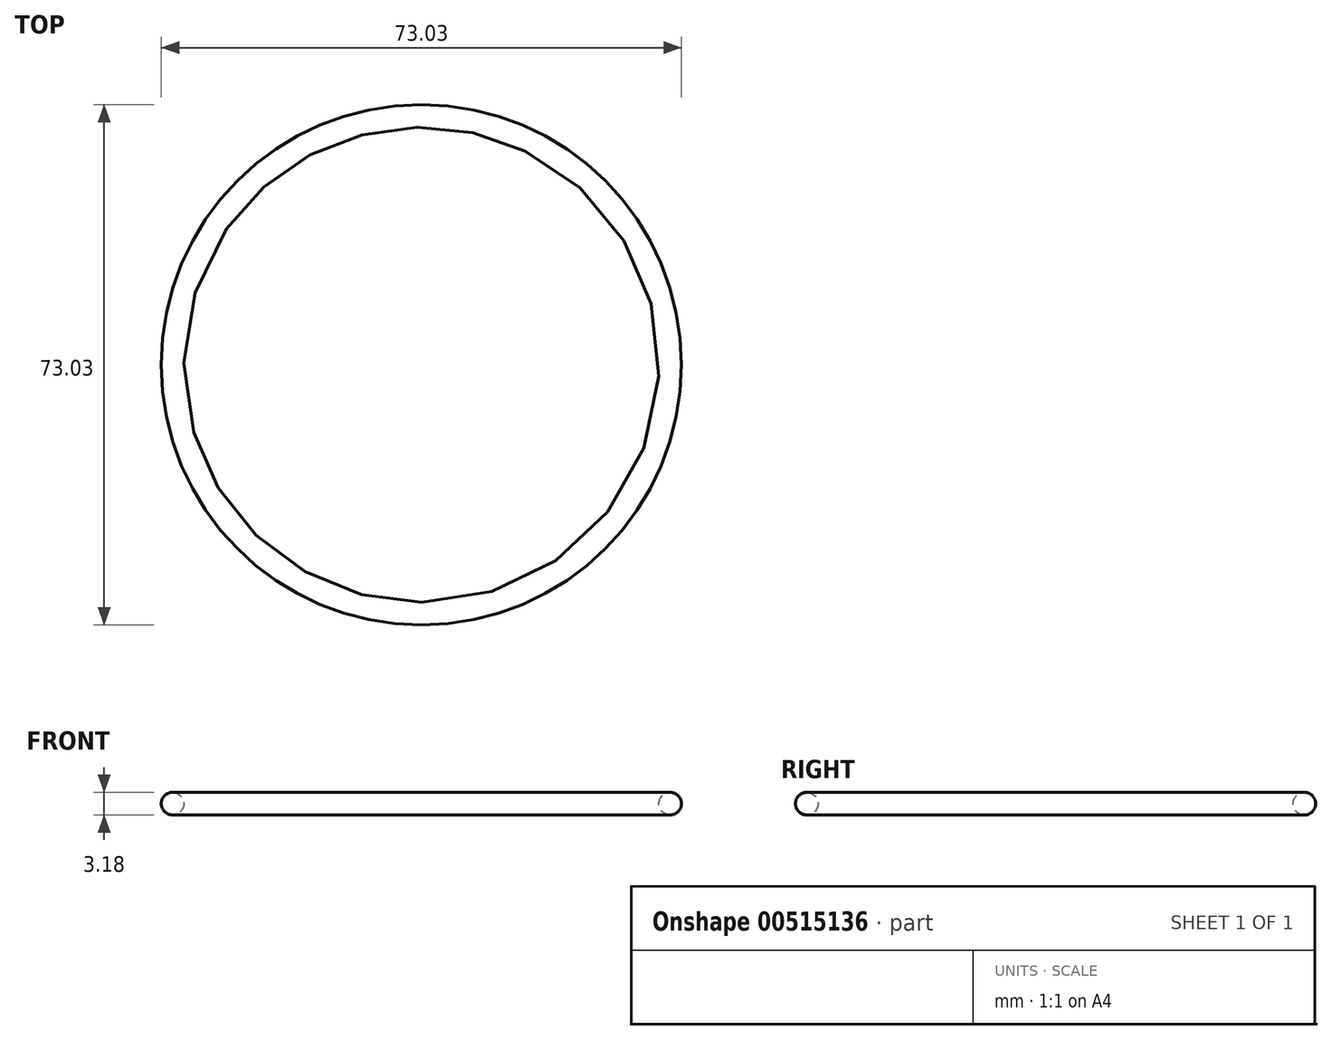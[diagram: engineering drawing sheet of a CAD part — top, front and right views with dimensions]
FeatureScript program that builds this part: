
annotation { "Feature Type Name" : "Feature", "Feature Type Description" : "" }
export const myFeature = defineFeature(function(context is Context, id is Id, definition is map)
    precondition{}
    {
        {
            var Q0;
            Q0=qCreatedBy(makeId("Right.planeOp"),FACE);
            var sketch = newSketch(context, id + "F0", { "sketchPlane" : qUnion([Q0])});
            skCircle(sketch, "E0", {"center": v(0, 0) * mm, "radius": 1.59 * mm});
            skSolve(sketch);
        }
        {
            var Q0;
            Q0=qCreatedBy(makeId("Top.planeOp"),FACE);
            var sketch = newSketch(context, id + "F1", { "sketchPlane" : qUnion([Q0])});
            skCircle(sketch, "E1", {"center": v(0.05, -34.92) * mm, "radius": 34.93 * mm});
            skPoint(sketch, "E1.first.point", {"position": v(0, 0) * mm});
            skPoint(sketch, "E1.second.point", {"position": v(0, -69.85) * mm});
            skPoint(sketch, "E1.third.point", {"position": v(-34.87, -34.82) * mm});
            skSolve(sketch);
        }
        {
            var Q0;
            Q0=makeQuery(id+"F0.imprint","IMPRINT",FACE,{"disambiguationData":[TD([[makeQuery(id+"F0.imprint","IMPRINT",EDGE,{"derivedFrom":sQuery(id+"F0.wireOp",EDGE,"E0")}),1.0]])]});
            var Q1;
            Q1=sQuery(id+"F1.wireOp",EDGE,"E1");
            sweep(context, id + "F2", {"profiles" : qUnion([Q0]), "path" : qUnion([Q1])});
        }
    });
